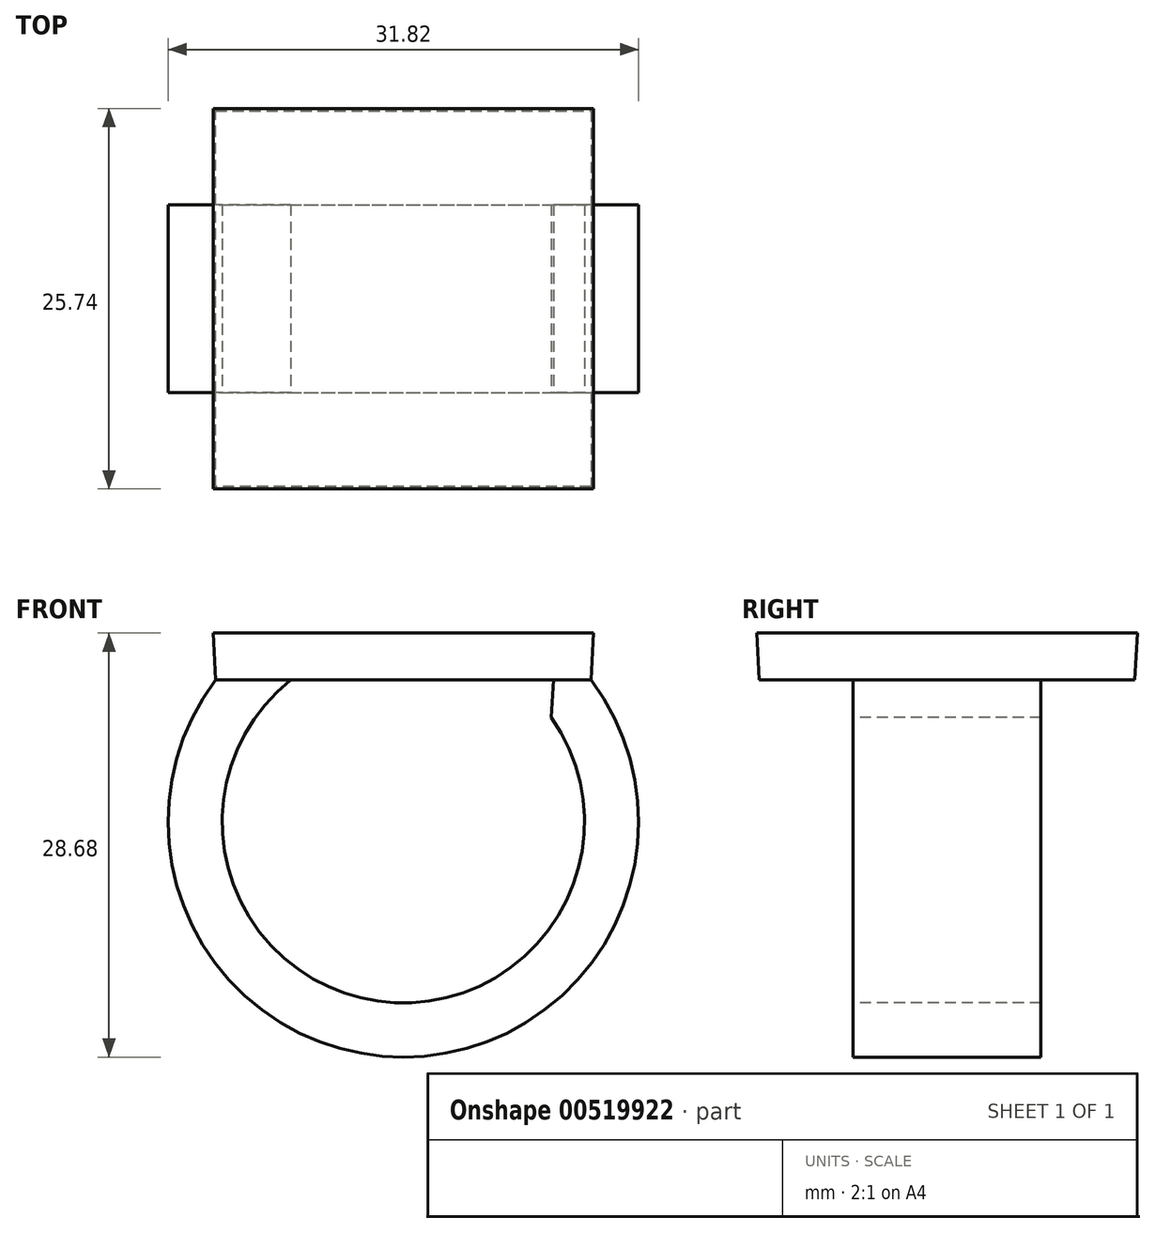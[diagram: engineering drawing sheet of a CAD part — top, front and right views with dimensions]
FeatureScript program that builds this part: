
annotation { "Feature Type Name" : "Feature", "Feature Type Description" : "" }
export const myFeature = defineFeature(function(context is Context, id is Id, definition is map)
    precondition{}
    {
        {
            var Q0;
            Q0=qCreatedBy(makeId("Top.planeOp"),FACE);
            var sketch = newSketch(context, id + "F0", { "sketchPlane" : qUnion([Q0])});
            skLineSegment(sketch, "E0.bottom", {"start": v(-12.7, -12.7) * mm, "end": v(12.7, -12.7) * mm});
            skLineSegment(sketch, "E0.top", {"start": v(-12.7, 12.7) * mm, "end": v(12.7, 12.7) * mm});
            skLineSegment(sketch, "E0.left", {"start": v(-12.7, -12.7) * mm, "end": v(-12.7, 12.7) * mm});
            skLineSegment(sketch, "E0.right", {"start": v(12.7, -12.7) * mm, "end": v(12.7, 12.7) * mm});
            skPoint(sketch, "E0.middle", {"position": v(0, 0) * mm});
            skSolve(sketch);
        }
        {
            var Q0;
            Q0 = qSketchRegion(id + "F0", true);
            extrude(context, id + "F1", {"entities" : qUnion([Q0]), "depth" : 3.17 * mm, "offsetDistance" : 25.4 * mm, "hasDraft" : true, "draftAngle" : 3 * degree});
        }
        {
            var Q0;
            Q0=qCreatedBy(makeId("Front.planeOp"),FACE);
            var sketch = newSketch(context, id + "F2", { "sketchPlane" : qUnion([Q0])});
            skArc(sketch, "E1", {"start": v(-10.16, 0) * mm, "mid": v(0, -23.56) * mm, "end": v(10.16, 0) * mm});
            skSolve(sketch);
        }
        {
            var Q0;
            Q0=makeQuery(id+"F1.opExtrude","CAP_FACE",FACE,{"disambiguationData":[OSD([sQuery(id+"F0.wireOp",EDGE,"E0.bottom"),sQuery(id+"F0.wireOp",EDGE,"E0.top"),sQuery(id+"F0.wireOp",EDGE,"E0.left"),sQuery(id+"F0.wireOp",EDGE,"E0.right")])],"isStart":true});
            var sketch = newSketch(context, id + "F3", { "sketchPlane" : qUnion([Q0])});
            skLineSegment(sketch, "E2.bottom", {"start": v(-7.62, -6.35) * mm, "end": v(-12.7, -6.35) * mm});
            skLineSegment(sketch, "E2.top", {"start": v(-7.62, 6.35) * mm, "end": v(-12.7, 6.35) * mm});
            skLineSegment(sketch, "E2.left", {"start": v(-7.62, -6.35) * mm, "end": v(-7.62, 6.35) * mm});
            skLineSegment(sketch, "E2.right", {"start": v(-12.7, -6.35) * mm, "end": v(-12.7, 6.35) * mm});
            skPoint(sketch, "E2.middle", {"position": v(-10.16, 0) * mm});
            skSolve(sketch);
        }
        {
            var Q0;
            Q0 = qSketchRegion(id + "F3", true);
            var Q1;
            Q1 = qConstructionFilter(qBodyType(qCreatedBy(id + "F2" ,EDGE), BodyType.WIRE), ConstructionObject.NO);
            sweep(context, id + "F4", {"operationType" : NewBodyOperationType.ADD, "profiles" : qUnion([Q0]), "path" : qUnion([Q1])});
        }
    });
